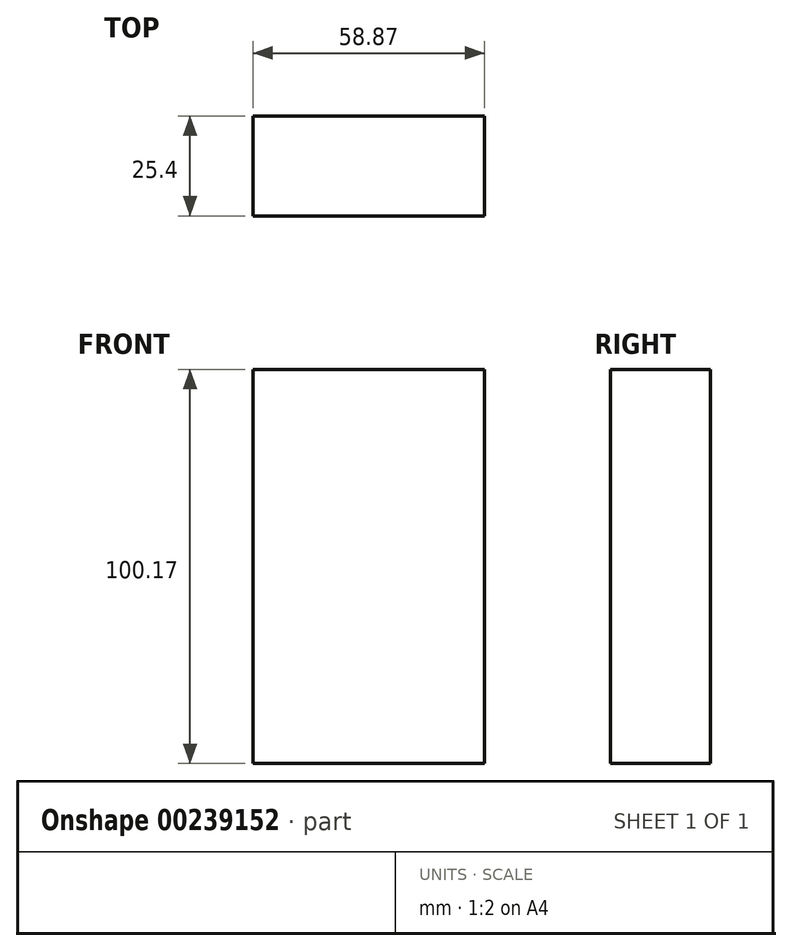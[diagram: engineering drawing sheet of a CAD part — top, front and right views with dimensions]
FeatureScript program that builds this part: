
annotation { "Feature Type Name" : "Feature", "Feature Type Description" : "" }
export const myFeature = defineFeature(function(context is Context, id is Id, definition is map)
    precondition{}
    {
        {
            var Q0;
            Q0=qCreatedBy(makeId("Front.planeOp"),FACE);
            var sketch = newSketch(context, id + "F0", { "sketchPlane" : qUnion([Q0])});
            skLineSegment(sketch, "E0.bottom", {"start": v(9.4, 39.01) * mm, "end": v(-49.46, 39.01) * mm});
            skLineSegment(sketch, "E0.top", {"start": v(9.4, -61.16) * mm, "end": v(-49.46, -61.16) * mm});
            skLineSegment(sketch, "E0.left", {"start": v(9.4, 39.01) * mm, "end": v(9.4, -61.16) * mm});
            skLineSegment(sketch, "E0.right", {"start": v(-49.46, 39.01) * mm, "end": v(-49.46, -61.16) * mm});
            skSolve(sketch);
        }
        {
            var Q0;
            Q0=makeQuery(id+"F0.imprint","IMPRINT",FACE,{"disambiguationData":[TD([[makeQuery(id+"F0.imprint","IMPRINT",EDGE,{"derivedFrom":sQuery(id+"F0.wireOp",EDGE,"E0.bottom")}),1.0]])]});
            extrude(context, id + "F1", {"entities" : qUnion([Q0]), "depth" : 25.4 * mm});
        }
    });
